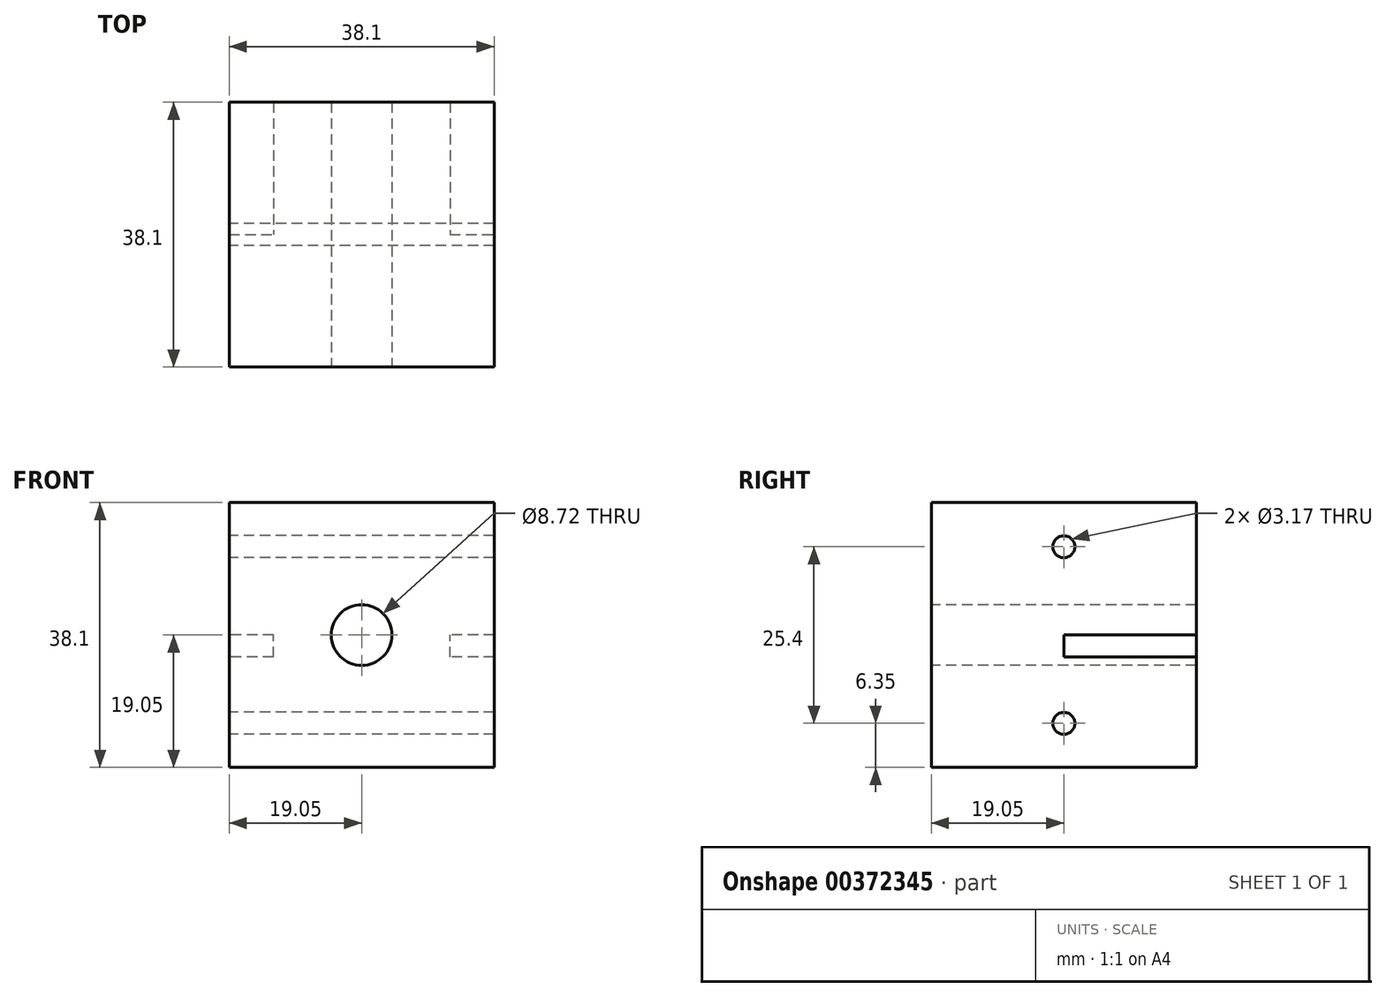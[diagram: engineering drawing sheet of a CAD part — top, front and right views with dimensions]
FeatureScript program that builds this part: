
annotation { "Feature Type Name" : "Feature", "Feature Type Description" : "" }
export const myFeature = defineFeature(function(context is Context, id is Id, definition is map)
    precondition{}
    {
        {
            var Q0;
            Q0=qCreatedBy(makeId("Front.planeOp"),FACE);
            var sketch = newSketch(context, id + "F0", { "sketchPlane" : qUnion([Q0])});
            skLineSegment(sketch, "E0.bottom", {"start": v(-19.05, 19.05) * mm, "end": v(19.05, 19.05) * mm});
            skLineSegment(sketch, "E0.top", {"start": v(-19.05, -19.05) * mm, "end": v(19.05, -19.05) * mm});
            skLineSegment(sketch, "E0.left", {"start": v(-19.05, 19.05) * mm, "end": v(-19.05, -19.05) * mm});
            skLineSegment(sketch, "E0.right", {"start": v(19.05, 19.05) * mm, "end": v(19.05, -19.05) * mm});
            skSolve(sketch);
        }
        {
            var Q0;
            Q0=qCreatedBy(makeId("Front.planeOp"),FACE);
            var sketch = newSketch(context, id + "F1", { "sketchPlane" : qUnion([Q0])});
            skCircle(sketch, "E1", {"center": v(0, 0) * mm, "radius": 4.36 * mm});
            skSolve(sketch);
        }
        {
            var Q0;
            Q0=qCreatedBy(makeId("Front.planeOp"),FACE);
            var sketch = newSketch(context, id + "F2", { "sketchPlane" : qUnion([Q0])});
            skLineSegment(sketch, "E2.bottom", {"start": v(-19.05, 0) * mm, "end": v(-12.7, 0) * mm});
            skLineSegment(sketch, "E2.top", {"start": v(-19.05, -3.18) * mm, "end": v(-12.7, -3.18) * mm});
            skLineSegment(sketch, "E2.left", {"start": v(-19.05, 0) * mm, "end": v(-19.05, -3.18) * mm});
            skLineSegment(sketch, "E2.right", {"start": v(-12.7, 0) * mm, "end": v(-12.7, -3.18) * mm});
            skSolve(sketch);
        }
        {
            var Q0;
            Q0=qCreatedBy(makeId("Front.planeOp"),FACE);
            var sketch = newSketch(context, id + "F3", { "sketchPlane" : qUnion([Q0])});
            skLineSegment(sketch, "E3.bottom", {"start": v(12.7, 0) * mm, "end": v(19.05, 0) * mm});
            skLineSegment(sketch, "E3.top", {"start": v(12.7, -3.17) * mm, "end": v(19.05, -3.17) * mm});
            skLineSegment(sketch, "E3.left", {"start": v(12.7, 0) * mm, "end": v(12.7, -3.17) * mm});
            skLineSegment(sketch, "E3.right", {"start": v(19.05, 0) * mm, "end": v(19.05, -3.17) * mm});
            skSolve(sketch);
        }
        {
            var Q0;
            Q0=qCreatedBy(makeId("Right.planeOp"),FACE);
            var sketch = newSketch(context, id + "F4", { "sketchPlane" : qUnion([Q0])});
            skCircle(sketch, "E4", {"center": v(0, 12.7) * mm, "radius": 1.59 * mm});
            skSolve(sketch);
        }
        {
            var Q0;
            Q0=qCreatedBy(makeId("Right.planeOp"),FACE);
            var sketch = newSketch(context, id + "F5", { "sketchPlane" : qUnion([Q0])});
            skCircle(sketch, "E5", {"center": v(0, -12.7) * mm, "radius": 1.59 * mm});
            skSolve(sketch);
        }
        {
            var Q0;
            Q0=qSketchRegion(id+"F0",true);
            extrude(context, id + "F6", {"entities" : qUnion([Q0]), "endBound" : BoundingType.SYMMETRIC, "depth" : 38.1 * mm});
        }
        {
            var Q0;
            Q0=qSketchRegion(id+"F1",true);
            extrude(context, id + "F7", {"entities" : qUnion([Q0]), "operationType" : NewBodyOperationType.REMOVE, "endBound" : BoundingType.SYMMETRIC, "oppositeDirection" : true, "depth" : 38.1 * mm});
        }
        {
            var Q0;
            Q0=qSketchRegion(id+"F2",true);
            var Q1;
            Q1=qSketchRegion(id+"F3",true);
            extrude(context, id + "F8", {"entities" : qUnion([Q0, Q1]), "operationType" : NewBodyOperationType.REMOVE, "endBound" : BoundingType.UP_TO_NEXT, "oppositeDirection" : true, "depth" : 12.7 * mm});
        }
        {
            var Q0;
            Q0=qSketchRegion(id+"F4",true);
            var Q1;
            Q1=qSketchRegion(id+"F5",true);
            extrude(context, id + "F9", {"entities" : qUnion([Q0, Q1]), "operationType" : NewBodyOperationType.REMOVE, "endBound" : BoundingType.SYMMETRIC, "depth" : 38.1 * mm});
        }
    });
